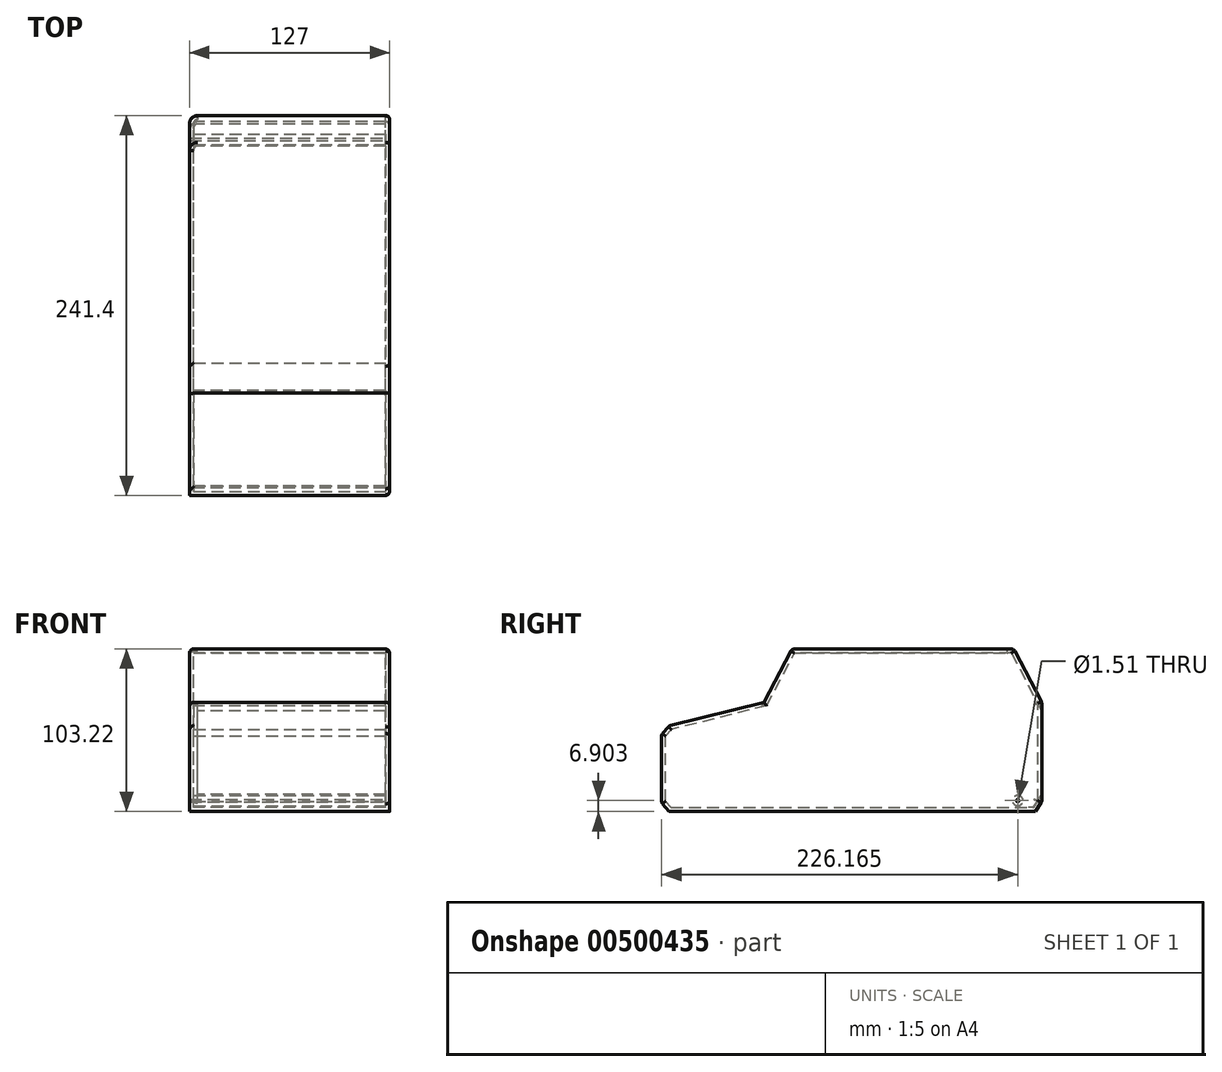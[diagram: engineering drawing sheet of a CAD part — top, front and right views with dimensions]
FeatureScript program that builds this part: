
annotation { "Feature Type Name" : "Feature", "Feature Type Description" : "" }
export const myFeature = defineFeature(function(context is Context, id is Id, definition is map)
    precondition{}
    {
        {
            var Q0;
            Q0=qCreatedBy(makeId("Right.planeOp"),FACE);
            var sketch = newSketch(context, id + "F0", { "sketchPlane" : qUnion([Q0])});
            skLineSegment(sketch, "E0", {"start": v(-161.59, 0) * mm, "end": v(71.06, 0) * mm});
            skLineSegment(sketch, "E1", {"start": v(-161.59, 0) * mm, "end": v(-166.36, 5.57) * mm});
            skLineSegment(sketch, "E2", {"start": v(-166.36, 5.57) * mm, "end": v(-166.36, 48.85) * mm});
            skLineSegment(sketch, "E3", {"start": v(-166.36, 48.85) * mm, "end": v(-161.59, 54.41) * mm});
            skLineSegment(sketch, "E4", {"start": v(-161.59, 54.41) * mm, "end": v(-101.41, 69.32) * mm});
            skLineSegment(sketch, "E5", {"start": v(-101.41, 69.32) * mm, "end": v(-83.6, 103.22) * mm});
            skLineSegment(sketch, "E6", {"start": v(-83.6, 103.22) * mm, "end": v(49.1, 103.22) * mm});
            skLineSegment(sketch, "E7", {"start": v(71.06, 0) * mm, "end": v(75.04, 6.15) * mm});
            skLineSegment(sketch, "E8", {"start": v(75.04, 6.15) * mm, "end": v(75.04, 69.32) * mm});
            skLineSegment(sketch, "E9", {"start": v(75.04, 69.32) * mm, "end": v(57.23, 103.22) * mm});
            skLineSegment(sketch, "E10", {"start": v(49.1, 103.22) * mm, "end": v(57.23, 103.22) * mm});
            skSolve(sketch);
        }
        {
            var Q0;
            Q0=makeQuery(id+"F0.imprint","IMPRINT",FACE,{"disambiguationData":[TD([[makeQuery(id+"F0.imprint","IMPRINT",EDGE,{"derivedFrom":sQuery(id+"F0.wireOp",EDGE,"E0")}),1.0]])]});
            extrude(context, id + "F1", {"entities" : qUnion([Q0]), "depth" : 127 * mm, "offsetDistance" : 25.4 * mm});
        }
        {
            var Q0;
            Q0=makeQuery(id+"F1.opExtrude","CAP_EDGE",EDGE,{"disambiguationData":[OSD([sQuery(id+"F0.wireOp",EDGE,"E3")])],"isStart":false});
            var Q1;
            Q1=makeQuery(id+"F1.opExtrude","CAP_EDGE",EDGE,{"disambiguationData":[OSD([sQuery(id+"F0.wireOp",EDGE,"E1")])],"isStart":false});
            fillet(context, id + "F2", {"entities" : qUnion([Q0, Q1]), "radius" : 2.54 * mm, "tangentPropagation" : true, "allowEdgeOverflow" : false});
        }
        {
            var Q0;
            Q0=makeQuery(id+"F1.opExtrude","CAP_EDGE",EDGE,{"disambiguationData":[OSD([sQuery(id+"F0.wireOp",EDGE,"E7")])],"isStart":false});
            var Q1;
            Q1=makeQuery(id+"F1.opExtrude","CAP_EDGE",EDGE,{"disambiguationData":[OSD([sQuery(id+"F0.wireOp",EDGE,"E9")])],"isStart":false});
            var Q2;
            Q2=makeQuery(id+"F1.opExtrude","CAP_EDGE",EDGE,{"disambiguationData":[OSD([sQuery(id+"F0.wireOp",EDGE,"E5")])],"isStart":false});
            fillet(context, id + "F3", {"entities" : qUnion([Q0, Q1, Q2]), "radius" : 2.54 * mm, "tangentPropagation" : true, "allowEdgeOverflow" : false});
        }
        {
            var Q0;
            Q0=makeQuery(id+"F1.opExtrude","SWEPT_EDGE",EDGE,{"disambiguationData":[OSD([sQuery(id+"F0.wireOp",EDGE,"E3"),sQuery(id+"F0.wireOp",EDGE,"E4")])]});
            var Q1;
            Q1=makeQuery(id+"F1.opExtrude","SWEPT_EDGE",EDGE,{"disambiguationData":[OSD([sQuery(id+"F0.wireOp",EDGE,"E2"),sQuery(id+"F0.wireOp",EDGE,"E3")])]});
            var Q2;
            Q2=makeQuery(id+"F1.opExtrude","SWEPT_EDGE",EDGE,{"disambiguationData":[OSD([sQuery(id+"F0.wireOp",EDGE,"E5"),sQuery(id+"F0.wireOp",EDGE,"E6")])]});
            var Q3;
            Q3=makeQuery(id+"F1.opExtrude","CAP_EDGE",EDGE,{"disambiguationData":[OSD([sQuery(id+"F0.wireOp",EDGE,"E4")])],"isStart":false});
            var Q4;
            Q4=makeQuery(id+"F1.opExtrude","CAP_EDGE",EDGE,{"disambiguationData":[OSD([sQuery(id+"F0.wireOp",EDGE,"E4")])],"isStart":true});
            var Q5;
            Q5=makeQuery(id+"F1.opExtrude","CAP_EDGE",EDGE,{"disambiguationData":[OSD([sQuery(id+"F0.wireOp",EDGE,"E6"),sQuery(id+"F0.wireOp",EDGE,"nDietInp-mlux-hqgZ-Dvvj-fCXYjEXwyFKL")])],"isStart":false});
            var Q6;
            Q6=makeQuery(id+"F1.opExtrude","CAP_EDGE",EDGE,{"disambiguationData":[OSD([sQuery(id+"F0.wireOp",EDGE,"E6"),sQuery(id+"F0.wireOp",EDGE,"nDietInp-mlux-hqgZ-Dvvj-fCXYjEXwyFKL")])],"isStart":true});
            var Q7;
            Q7=makeQuery(id+"F1.opExtrude","SWEPT_EDGE",EDGE,{"disambiguationData":[OSD([sQuery(id+"F0.wireOp",EDGE,"E9"),sQuery(id+"F0.wireOp",EDGE,"nDietInp-mlux-hqgZ-Dvvj-fCXYjEXwyFKL")])]});
            fillet(context, id + "F4", {"entities" : qUnion([Q0, Q1, Q2, Q3, Q4, Q5, Q6, Q7]), "radius" : 2.54 * mm, "tangentPropagation" : true, "allowEdgeOverflow" : false});
        }
        {
            var Q0;
            Q0=makeQuery(id+"F1.opExtrude","CAP_FACE",FACE,{"disambiguationData":[OSD([sQuery(id+"F0.wireOp",EDGE,"E0"),sQuery(id+"F0.wireOp",EDGE,"E1"),sQuery(id+"F0.wireOp",EDGE,"E2"),sQuery(id+"F0.wireOp",EDGE,"E3"),sQuery(id+"F0.wireOp",EDGE,"E4"),sQuery(id+"F0.wireOp",EDGE,"E5"),sQuery(id+"F0.wireOp",EDGE,"E6"),sQuery(id+"F0.wireOp",EDGE,"E7"),sQuery(id+"F0.wireOp",EDGE,"E8"),sQuery(id+"F0.wireOp",EDGE,"E9"),sQuery(id+"F0.wireOp",EDGE,"nDietInp-mlux-hqgZ-Dvvj-fCXYjEXwyFKL")])],"isStart":false});
            var sketch = newSketch(context, id + "F5", { "sketchPlane" : qUnion([Q0])});
            skLineSegment(sketch, "E11", {"start": v(72.5, 6.9) * mm, "end": v(59.8, 6.9) * mm});
            skCircle(sketch, "E12", {"center": v(59.8, 6.9) * mm, "radius": 0.76 * mm});
            skSolve(sketch);
        }
        {
            var Q0;
            {var subQ0=sQuery(id+"F0.wireOp",EDGE,"E7");Q0=makeQuery(id+"F3.opFillet","BLEND_EDGE",EDGE,{"blendedFrom":[makeQuery(id+"F1.opExtrude","CAP_EDGE",EDGE,{"disambiguationData":[OSD([subQ0])],"isStart":false}),makeQuery(id+"F1.opExtrude","CAP_FACE",FACE,{"disambiguationData":[OSD([sQuery(id+"F0.wireOp",EDGE,"E0"),sQuery(id+"F0.wireOp",EDGE,"E1"),sQuery(id+"F0.wireOp",EDGE,"E2"),sQuery(id+"F0.wireOp",EDGE,"E3"),sQuery(id+"F0.wireOp",EDGE,"E4"),sQuery(id+"F0.wireOp",EDGE,"E5"),sQuery(id+"F0.wireOp",EDGE,"E6"),subQ0,sQuery(id+"F0.wireOp",EDGE,"E8"),sQuery(id+"F0.wireOp",EDGE,"E9"),sQuery(id+"F0.wireOp",EDGE,"nDietInp-mlux-hqgZ-Dvvj-fCXYjEXwyFKL")])],"isStart":false})],"blendedInto":[makeQuery(id+"F1.opExtrude","CAP_FACE",FACE,{"disambiguationData":[OSD([sQuery(id+"F0.wireOp",EDGE,"E0"),sQuery(id+"F0.wireOp",EDGE,"E1"),sQuery(id+"F0.wireOp",EDGE,"E2"),sQuery(id+"F0.wireOp",EDGE,"E3"),sQuery(id+"F0.wireOp",EDGE,"E4"),sQuery(id+"F0.wireOp",EDGE,"E5"),sQuery(id+"F0.wireOp",EDGE,"E6"),subQ0,sQuery(id+"F0.wireOp",EDGE,"E8"),sQuery(id+"F0.wireOp",EDGE,"E9"),sQuery(id+"F0.wireOp",EDGE,"nDietInp-mlux-hqgZ-Dvvj-fCXYjEXwyFKL")])],"isStart":false})]});}
            var Q1;
            Q1=makeQuery(id+"F1.opExtrude","CAP_EDGE",EDGE,{"disambiguationData":[OSD([sQuery(id+"F0.wireOp",EDGE,"E7")])],"isStart":true});
            fillet(context, id + "F6", {"entities" : qUnion([Q0, Q1]), "radius" : 5.08 * mm, "tangentPropagation" : true, "allowEdgeOverflow" : false});
        }
        {
            var Q0;
            Q0 = qSketchRegion(id + "F5", true);
            extrude(context, id + "F7", {"entities" : qUnion([Q0]), "operationType" : NewBodyOperationType.REMOVE, "oppositeDirection" : true, "depth" : 254 * mm, "offsetDistance" : 25.4 * mm});
        }
        {
            var Q0;
            Q0=makeQuery(id+"F1.opExtrude","SWEPT_FACE",FACE,{"disambiguationData":[OSD([sQuery(id+"F0.wireOp",EDGE,"E8")])]});
            shell(context, id + "F8", {"entities" : qUnion([Q0]), "thickness" : 2.54 * mm});
        }
    });
